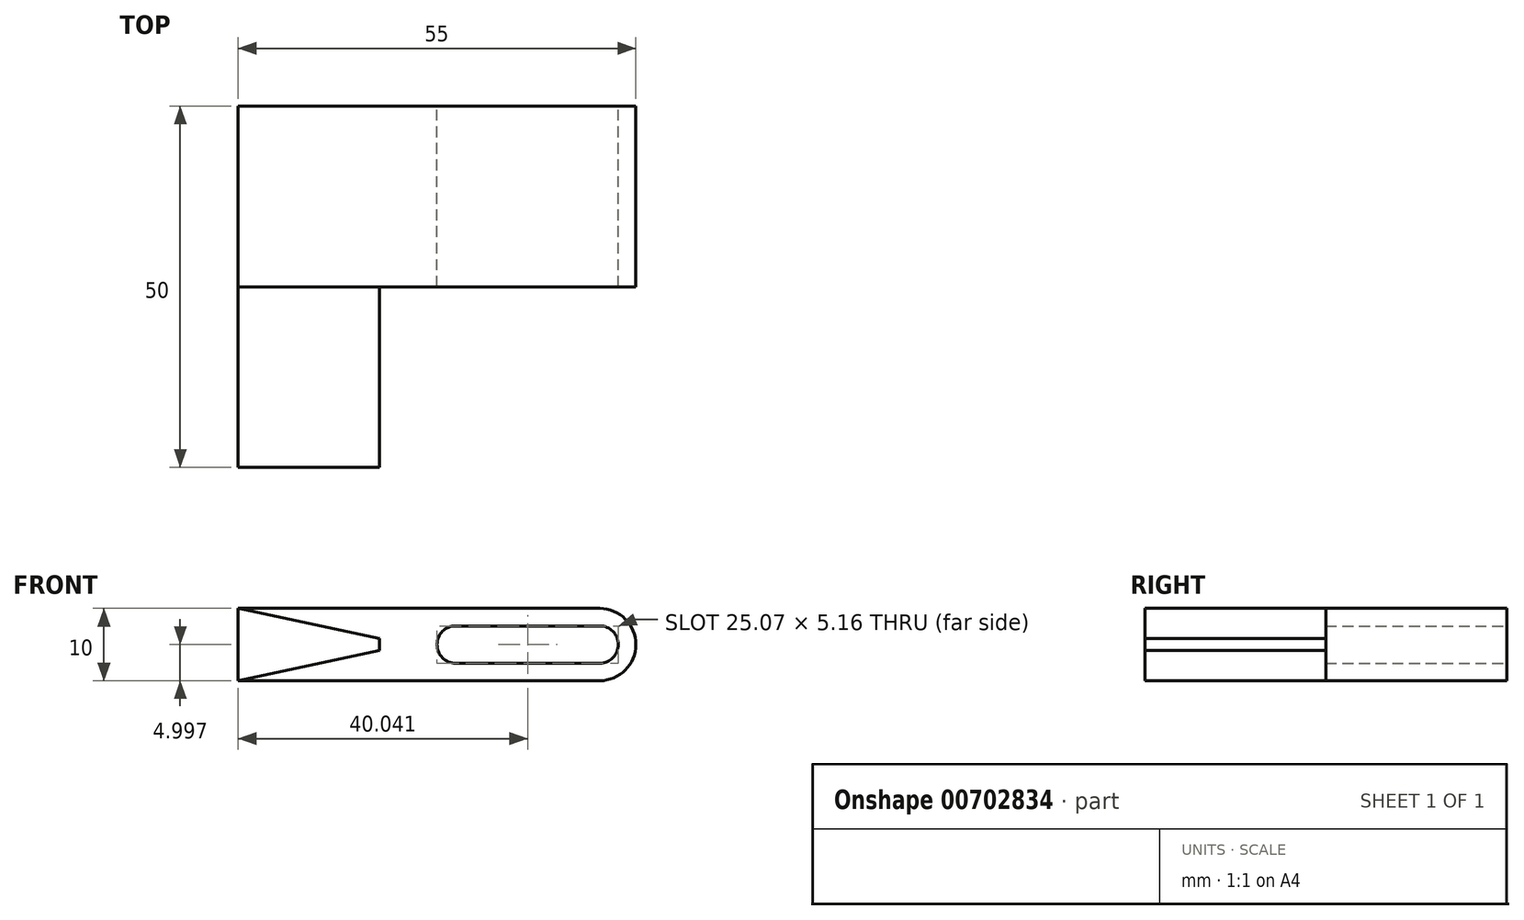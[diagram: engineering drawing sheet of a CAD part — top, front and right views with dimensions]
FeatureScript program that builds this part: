
annotation { "Feature Type Name" : "Feature", "Feature Type Description" : "" }
export const myFeature = defineFeature(function(context is Context, id is Id, definition is map)
    precondition{}
    {
        {
            var Q0;
            Q0=qCreatedBy(makeId("Front.planeOp"),FACE);
            var sketch = newSketch(context, id + "F0", { "sketchPlane" : qUnion([Q0])});
            skLineSegment(sketch, "E0", {"start": v(-47.63, 5.87) * mm, "end": v(-47.63, -4.13) * mm});
            skLineSegment(sketch, "E1", {"start": v(-47.63, -4.13) * mm, "end": v(2.37, -4.13) * mm});
            skLineSegment(sketch, "E2", {"start": v(2.37, 5.87) * mm, "end": v(-47.63, 5.87) * mm});
            skArc(sketch, "E3", {"start": v(2.37, -4.13) * mm, "mid": v(7.37, 0.87) * mm, "end": v(2.37, 5.87) * mm});
            skArc(sketch, "E4", {"start": v(2.37, -1.72) * mm, "mid": v(4.95, 0.87) * mm, "end": v(2.37, 3.45) * mm});
            skArc(sketch, "E5", {"start": v(-17.54, 3.45) * mm, "mid": v(-20.13, 0.87) * mm, "end": v(-17.54, -1.72) * mm});
            skLineSegment(sketch, "E6", {"start": v(-17.54, 3.45) * mm, "end": v(2.37, 3.45) * mm});
            skLineSegment(sketch, "E7", {"start": v(2.37, -1.72) * mm, "end": v(-17.54, -1.72) * mm});
            skSolve(sketch);
        }
        {
            var Q0;
            Q0 = qSketchRegion(id + "F0", true);
            extrude(context, id + "F1", {"entities" : qUnion([Q0]), "depth" : 25 * mm, "offsetDistance" : 25 * mm});
        }
        {
            var Q0;
            Q0=makeQuery(id+"F1.opExtrude","CAP_FACE",FACE,{"disambiguationData":[OSD([sQuery(id+"F0.wireOp",EDGE,"E0"),sQuery(id+"F0.wireOp",EDGE,"E1"),sQuery(id+"F0.wireOp",EDGE,"E2"),sQuery(id+"F0.wireOp",EDGE,"E3"),sQuery(id+"F0.wireOp",EDGE,"E4"),sQuery(id+"F0.wireOp",EDGE,"E5"),sQuery(id+"F0.wireOp",EDGE,"E6"),sQuery(id+"F0.wireOp",EDGE,"E7")])],"isStart":false});
            var sketch = newSketch(context, id + "F2", { "sketchPlane" : qUnion([Q0])});
            skLineSegment(sketch, "E8", {"start": v(-47.63, 5.87) * mm, "end": v(-47.63, -4.13) * mm});
            skLineSegment(sketch, "E9", {"start": v(-47.63, -4.13) * mm, "end": v(-28.07, 0.03) * mm});
            skLineSegment(sketch, "E10", {"start": v(-28.07, 0.03) * mm, "end": v(-28.07, 1.7) * mm});
            skLineSegment(sketch, "E11", {"start": v(-28.07, 1.7) * mm, "end": v(-47.63, 5.87) * mm});
            skSolve(sketch);
        }
        {
            var Q0;
            Q0 = qSketchRegion(id + "F2", true);
            extrude(context, id + "F3", {"entities" : qUnion([Q0]), "operationType" : NewBodyOperationType.ADD, "depth" : 25 * mm, "offsetDistance" : 25 * mm});
        }
    });
